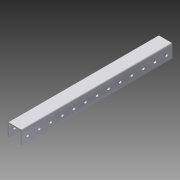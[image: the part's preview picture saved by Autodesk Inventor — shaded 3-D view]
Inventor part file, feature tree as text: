
AUTODESK INVENTOR PART (.ipt)
format: ipt  version: 2015 (Build 190159000, 159)  size: 153,600 bytes
history: native  units: in
note: dims shown in document units (in); Inventor stores cm internally (conversion verified against a paired STEP export)
features: extrude x2, sketch x2, pattern_linear x1
ambient origin geometry x8: Origin, YZ Plane, XZ Plane, XY Plane, X Axis, Y Axis, Z Axis, Center Point
bodies: Solid1 (feature_tree)
feature tree (5):
  extrude  "Extrusion1"  Depth=13.0in
  extrude  "Extrusion4"  Depth=0.5in
  pattern_linear  "Rectangular Pattern3"  Spacing1=0.0in  [1 undecoded]
  sketch  "Sketch1"  dims[d0=1.13in d1=1.25in d2=0.125in d3=0.125in d4=0.125in d5=13.0in]
  sketch  "Sketch4"  dims[d6=0.0in d35=0.5in d36=0.0in d37=0.25in d38=1.0in d39=0.0in d40=3.937in d42=1.0in d43=3.937in d45=1.0in]
note: 1 required parameter value undecoded (feature->parameter linkage not recoverable at this tier; creation-order binding heuristic only, values carry confidence <= 0.55)
